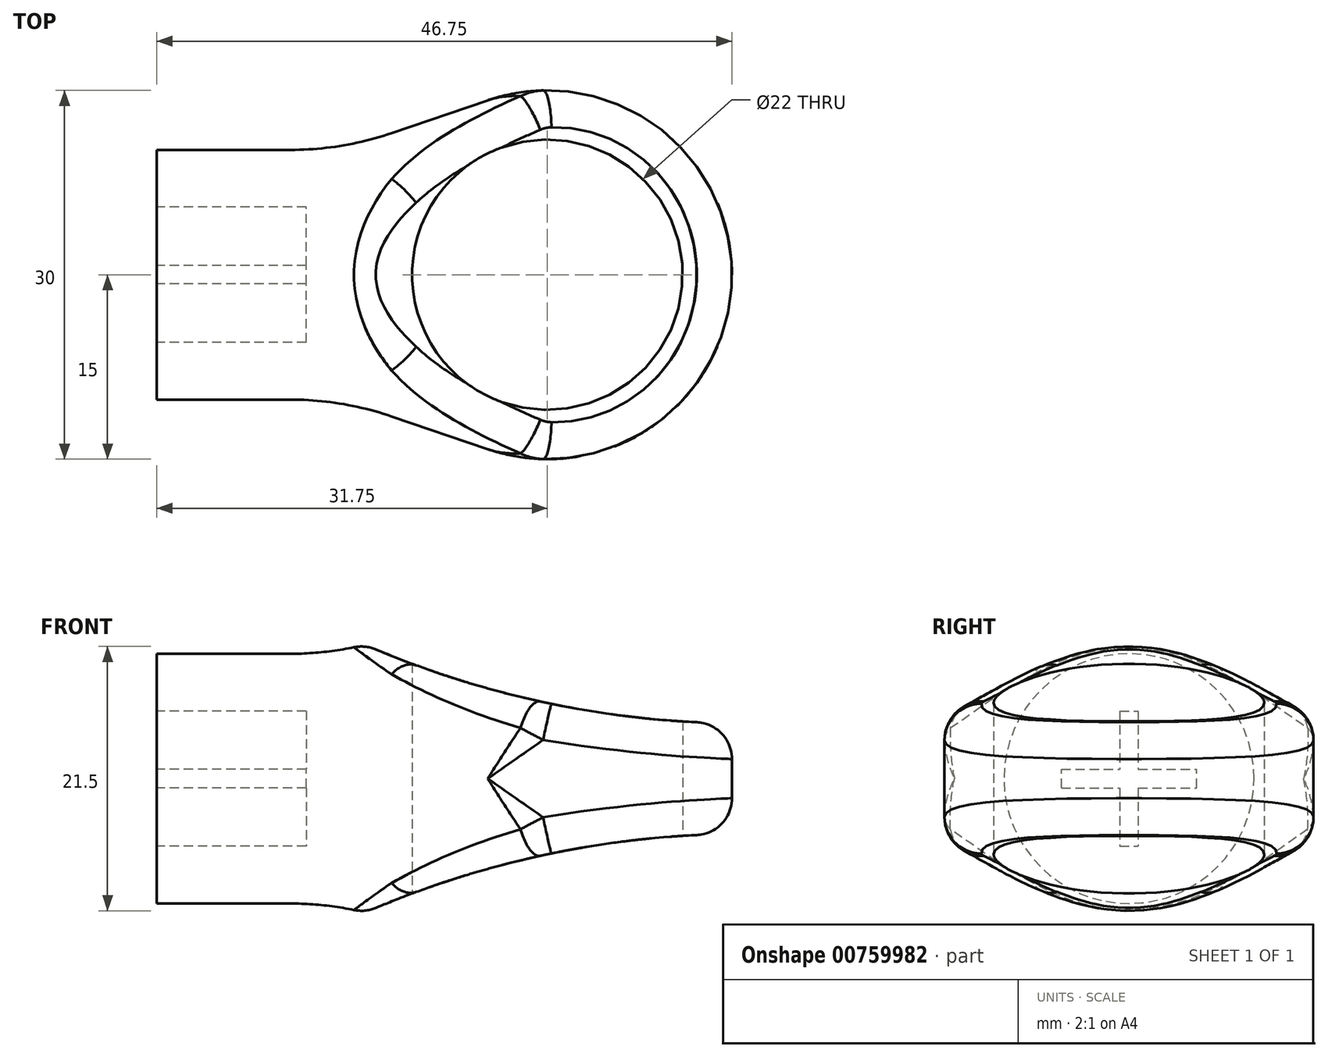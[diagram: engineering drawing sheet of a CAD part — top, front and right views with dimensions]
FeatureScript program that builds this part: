
annotation { "Feature Type Name" : "Feature", "Feature Type Description" : "" }
export const myFeature = defineFeature(function(context is Context, id is Id, definition is map)
    precondition{}
    {
        {
            var Q0;
            Q0=qCreatedBy(makeId("Top.planeOp"),FACE);
            var sketch = newSketch(context, id + "F0", { "sketchPlane" : qUnion([Q0])});
            skCircle(sketch, "E0", {"center": v(0, 0) * mm, "radius": 11 * mm});
            skCircle(sketch, "E1", {"center": v(0, 0) * mm, "radius": 15 * mm});
            skSolve(sketch);
        }
        {
            var Q0;
            Q0=makeQuery(id+"F0.imprint","IMPRINT",FACE,{"disambiguationData":[TD([[makeQuery(id+"F0.imprint","IMPRINT",EDGE,{"derivedFrom":sQuery(id+"F0.wireOp",EDGE,"E0")}),-1.0]])]});
            extrude(context, id + "F1", {"entities" : qUnion([Q0]), "endBound" : BoundingType.SYMMETRIC, "depth" : 25.4 * mm, "offsetDistance" : 25.4 * mm, "hasSecondDirection" : true, "secondDirectionOppositeDirection" : true, "secondDirectionDepth" : 4 * mm});
        }
        {
            var Q0;
            Q0=qCreatedBy(makeId("Front.planeOp"),FACE);
            var sketch = newSketch(context, id + "F2", { "sketchPlane" : qUnion([Q0])});
            skLineSegment(sketch, "E2.bottom", {"start": v(-11, 0) * mm, "end": v(-31.75, 0) * mm});
            skLineSegment(sketch, "E2.top", {"start": v(-16.66, 10.16) * mm, "end": v(-31.75, 10.16) * mm});
            skLineSegment(sketch, "E2.right", {"start": v(-31.75, 0) * mm, "end": v(-31.75, 10.16) * mm});
            skLineSegment(sketch, "E3", {"start": v(-11, 4.5) * mm, "end": v(-16.66, 10.16) * mm});
            skLineSegment(sketch, "E4", {"start": v(0, 4.5) * mm, "end": v(-11, 4.5) * mm, "construction": true});
            skLineSegment(sketch, "E5", {"start": v(-11, 4.5) * mm, "end": v(-11, 0) * mm});
            skSolve(sketch);
        }
        {
            var Q0;
            Q0=makeQuery(id+"F2.imprint","IMPRINT",FACE,{"disambiguationData":[TD([[makeQuery(id+"F2.imprint","IMPRINT",EDGE,{"derivedFrom":sQuery(id+"F2.wireOp",EDGE,"E2.bottom")}),-1.0]])]});
            var Q1;
            Q1=sQuery(id+"F2.wireOp",EDGE,"E2.bottom");
            revolve(context, id + "F3", {"operationType" : NewBodyOperationType.ADD, "surfaceOperationType" : NewSurfaceOperationType.NEW, "entities" : qUnion([Q0]), "axis" : qUnion([Q1]), "revolveType" : RevolveType.FULL});
        }
        {
            var Q0;
            Q0=qCreatedBy(makeId("Top.planeOp"),FACE);
            var sketch = newSketch(context, id + "F4", { "sketchPlane" : qUnion([Q0])});
            skLineSegment(sketch, "E6", {"start": v(-31.75, 10.16) * mm, "end": v(-16.66, 10.16) * mm, "construction": true});
            skLineSegment(sketch, "E7", {"start": v(-16.66, 10.16) * mm, "end": v(-13.35, 6.85) * mm, "construction": true});
            skArc(sketch, "E8.0.0", {"start": v(-13.84, 5.8) * mm, "mid": v(-15, 0) * mm, "end": v(-13.84, -5.8) * mm, "construction": true});
            skArc(sketch, "E8.0.2", {"start": v(-13.84, -5.8) * mm, "mid": v(15, 0) * mm, "end": v(-13.84, 5.8) * mm, "construction": true});
            skLineSegment(sketch, "E9", {"start": v(-16.66, 10.16) * mm, "end": v(-4.85, 14.2) * mm});
            skLineSegment(sketch, "E10", {"start": v(-16.66, 10.16) * mm, "end": v(-13.35, 6.85) * mm});
            skArc(sketch, "E11", {"start": v(-4.85, 14.2) * mm, "mid": v(-9.81, 11.35) * mm, "end": v(-13.35, 6.85) * mm});
            skLineSegment(sketch, "E12", {"start": v(-13.35, -6.85) * mm, "end": v(-16.66, -10.16) * mm, "construction": true});
            skLineSegment(sketch, "E13", {"start": v(-16.66, -10.16) * mm, "end": v(-4.85, -14.2) * mm});
            skLineSegment(sketch, "E14", {"start": v(-13.35, -6.85) * mm, "end": v(-16.66, -10.16) * mm});
            skArc(sketch, "E15", {"start": v(-13.35, -6.85) * mm, "mid": v(-9.81, -11.35) * mm, "end": v(-4.85, -14.2) * mm});
            skLineSegment(sketch, "E16", {"start": v(-16.66, -10.16) * mm, "end": v(-31.75, -10.16) * mm, "construction": true});
            skLineSegment(sketch, "E17", {"start": v(-16.66, 10.16) * mm, "end": v(-16.66, -10.16) * mm});
            skLineSegment(sketch, "E18", {"start": v(-13.35, 6.85) * mm, "end": v(-13.35, -6.85) * mm});
            skSolve(sketch);
        }
        {
            var Q0;
            Q0 = qSketchRegion(id + "F4", true);
            extrude(context, id + "F5", {"entities" : qUnion([Q0]), "operationType" : NewBodyOperationType.ADD, "endBound" : BoundingType.SYMMETRIC, "depth" : 25.4 * mm, "offsetDistance" : 25.4 * mm});
        }
        {
            var Q0;
            Q0=qCreatedBy(makeId("Top.planeOp"),FACE);
            var sketch = newSketch(context, id + "F6", { "sketchPlane" : qUnion([Q0])});
            skLineSegment(sketch, "E19", {"start": v(-31.75, 10.16) * mm, "end": v(-16.66, 10.16) * mm, "construction": true});
            skLineSegment(sketch, "E20.0.0", {"start": v(-16.66, -10.16) * mm, "end": v(-4.85, -14.2) * mm, "construction": true});
            skArc(sketch, "E20.0.1", {"start": v(-4.85, -14.2) * mm, "mid": v(15, 0) * mm, "end": v(-4.85, 14.2) * mm, "construction": true});
            skLineSegment(sketch, "E20.0.2", {"start": v(-4.85, 14.2) * mm, "end": v(-16.66, 10.16) * mm, "construction": true});
            skLineSegment(sketch, "E20.0.3", {"start": v(-16.66, 10.16) * mm, "end": v(-16.66, 9.1) * mm, "construction": true});
            skFitSpline(sketch, "E20.0.4", {"points": [v(-16.66, 9.1) * mm, v(-16.05, 8.43) * mm, v(-15.16, 7.4) * mm, v(-14, 6) * mm, v(-13.16, 4.93) * mm, v(-12.38, 3.81) * mm, v(-11.8, 2.84) * mm, v(-11.42, 2.01) * mm, v(-11.19, 1.36) * mm, v(-11.04, 0.7) * mm, v(-11, 0.23) * mm, v(-11, 0) * mm], "construction": true});
            skCircle(sketch, "E20.0.5", {"center": v(0, 0) * mm, "radius": 11 * mm, "construction": true});
            skFitSpline(sketch, "E20.0.6", {"points": [v(-11, 0) * mm, v(-11, -0.23) * mm, v(-11.03, -0.68) * mm, v(-11.18, -1.35) * mm, v(-11.41, -2) * mm, v(-11.8, -2.82) * mm, v(-12.37, -3.8) * mm, v(-13.16, -4.92) * mm, v(-14, -6) * mm, v(-15.15, -7.4) * mm, v(-16.05, -8.43) * mm, v(-16.66, -9.1) * mm], "construction": true});
            skLineSegment(sketch, "E20.0.7", {"start": v(-16.66, -9.1) * mm, "end": v(-16.66, -10.16) * mm, "construction": true});
            skLineSegment(sketch, "E21", {"start": v(-16.66, 10.16) * mm, "end": v(1.72, 16.44) * mm});
            skLineSegment(sketch, "E22", {"start": v(1.72, 16.44) * mm, "end": v(1.72, 19.36) * mm});
            skLineSegment(sketch, "E23", {"start": v(1.72, 19.36) * mm, "end": v(-16.66, 19.36) * mm});
            skLineSegment(sketch, "E24", {"start": v(-16.66, 19.36) * mm, "end": v(-16.66, 10.16) * mm});
            skLineSegment(sketch, "E25", {"start": v(0, 0) * mm, "end": v(-37.39, 0) * mm});
            skSolve(sketch);
        }
        {
            var Q0;
            Q0=makeQuery(id+"F6.imprint","IMPRINT",FACE,{"disambiguationData":[TD([[makeQuery(id+"F6.imprint","IMPRINT",EDGE,{"derivedFrom":sQuery(id+"F6.wireOp",EDGE,"E21")}),1.0]])]});
            var Q1;
            Q1=sQuery(id+"F6.wireOp",EDGE,"E25");
            revolve(context, id + "F7", {"operationType" : NewBodyOperationType.REMOVE, "surfaceOperationType" : NewSurfaceOperationType.NEW, "entities" : qUnion([Q0]), "axis" : qUnion([Q1]), "revolveType" : RevolveType.FULL, "oppositeDirection" : true});
        }
        {
            var Q0;
            Q0=makeQuery(id+"F3.opRevolve","SWEPT_FACE",FACE,{"disambiguationData":[OSD([sQuery(id+"F2.wireOp",EDGE,"E2.right")])]});
            var sketch = newSketch(context, id + "F8", { "sketchPlane" : qUnion([Q0])});
            skLineSegment(sketch, "E26.bottom", {"start": v(5.5, -0.75) * mm, "end": v(-5.5, -0.75) * mm});
            skLineSegment(sketch, "E26.top", {"start": v(5.5, 0.75) * mm, "end": v(-5.5, 0.75) * mm});
            skLineSegment(sketch, "E26.left", {"start": v(5.5, -0.75) * mm, "end": v(5.5, 0.75) * mm});
            skLineSegment(sketch, "E26.right", {"start": v(-5.5, -0.75) * mm, "end": v(-5.5, 0.75) * mm});
            skPoint(sketch, "E26.middle", {"position": v(0, 0) * mm});
            skLineSegment(sketch, "E27.bottom", {"start": v(0.75, 5.5) * mm, "end": v(-0.75, 5.5) * mm});
            skLineSegment(sketch, "E27.top", {"start": v(0.75, -5.5) * mm, "end": v(-0.75, -5.5) * mm});
            skLineSegment(sketch, "E27.left", {"start": v(0.75, 5.5) * mm, "end": v(0.75, -5.5) * mm});
            skLineSegment(sketch, "E27.right", {"start": v(-0.75, 5.5) * mm, "end": v(-0.75, -5.5) * mm});
            skSolve(sketch);
        }
        {
            var Q0;
            Q0 = qSketchRegion(id + "F8", true);
            extrude(context, id + "F9", {"entities" : qUnion([Q0]), "operationType" : NewBodyOperationType.REMOVE, "oppositeDirection" : true, "depth" : 12.14 * mm, "offsetDistance" : 25.4 * mm});
        }
        {
            var Q0;
            {var subQ0=sQuery(id+"F2.wireOp",EDGE,"E3");var subQ1=makeQuery(id+"F3.opRevolve","SWEPT_FACE",FACE,{"disambiguationData":[OSD([subQ0])]});var subQ2=sQuery(id+"F2.wireOp",EDGE,"E2.top");var subQ3=makeQuery(id+"F3.opRevolve","SWEPT_FACE",FACE,{"disambiguationData":[OSD([subQ2])]});var subQ4=sQuery(id+"F4.wireOp",EDGE,"E9");var subQ5=makeQuery(id+"F5.opExtrude","SWEPT_FACE",FACE,{"disambiguationData":[OSD([subQ4])]});var subQ6=sQuery(id+"F0.wireOp",EDGE,"E1");var subQ7=sQuery(id+"F0.wireOp",EDGE,"E0");var subQ8=sQuery(id+"F4.wireOp",EDGE,"E17");var subQ9=makeQuery(id+"F5.opExtrude","SWEPT_FACE",FACE,{"disambiguationData":[OSD([subQ8])]});var subQ10=sQuery(id+"F4.wireOp",EDGE,"E18");var subQ11=sQuery(id+"F4.wireOp",EDGE,"E15");var subQ12=sQuery(id+"F4.wireOp",EDGE,"E13");var subQ13=sQuery(id+"F4.wireOp",EDGE,"E11");var subQ14=makeQuery(id+"F3.opRevolve","SWEPT_EDGE",EDGE,{"disambiguationData":[OSD([subQ2,subQ0])]});Q0=makeQuery(id+"F7.boolean.opBoolean","MERGE",EDGE,{"derivedFrom":[makeQuery(id+"F5.boolean.opBoolean","SPLIT",EDGE,{"disambiguationData":[topologyDisambiguationEdgeConnected([subQ3,subQ9]),TD([makeQuery(id+"F1.opExtrude","CAP_FACE",FACE,{"disambiguationData":[OSD([subQ7,subQ6])],"isStart":true}),subQ3,subQ1,subQ5,makeQuery(id+"F5.opExtrude","CAP_FACE",FACE,{"disambiguationData":[OSD([subQ4,subQ13,subQ12,subQ11,subQ10,subQ8])],"isStart":true}),subQ9])],"derivedFrom":subQ14}),makeQuery(id+"F5.boolean.opBoolean","SPLIT",EDGE,{"disambiguationData":[topologyDisambiguationEdgeConnected([subQ3,subQ9]),TD([makeQuery(id+"F1.opExtrude","CAP_FACE",FACE,{"disambiguationData":[OSD([subQ7,subQ6])],"isStart":false}),subQ3,subQ1,subQ5,makeQuery(id+"F5.opExtrude","CAP_FACE",FACE,{"disambiguationData":[OSD([subQ4,subQ13,subQ12,subQ11,subQ10,subQ8])],"isStart":false}),subQ9])],"derivedFrom":subQ14}),makeQuery(id+"F7.opRevolve","SWEPT_EDGE",EDGE,{"disambiguationData":[OSD([sQuery(id+"F6.wireOp",EDGE,"E21"),sQuery(id+"F6.wireOp",EDGE,"E24")])]})]});}
            var Q1;
            {var subQ0=sQuery(id+"F4.wireOp",EDGE,"E17");var subQ1=sQuery(id+"F4.wireOp",EDGE,"E18");var subQ2=sQuery(id+"F4.wireOp",EDGE,"E15");var subQ3=sQuery(id+"F4.wireOp",EDGE,"E13");var subQ4=sQuery(id+"F4.wireOp",EDGE,"E11");var subQ5=sQuery(id+"F4.wireOp",EDGE,"E9");var subQ6=sQuery(id+"F2.wireOp",EDGE,"E3");var subQ7=makeQuery(id+"F3.opRevolve","SWEPT_FACE",FACE,{"disambiguationData":[OSD([subQ6])]});var subQ8=sQuery(id+"F2.wireOp",EDGE,"E2.top");var subQ9=makeQuery(id+"F3.opRevolve","SWEPT_FACE",FACE,{"disambiguationData":[OSD([subQ8])]});var subQ10=sQuery(id+"F0.wireOp",EDGE,"E1");var subQ11=sQuery(id+"F0.wireOp",EDGE,"E0");var subQ12=makeQuery(id+"F5.opExtrude","SWEPT_FACE",FACE,{"disambiguationData":[OSD([subQ0])]});var subQ13=makeQuery(id+"F5.opExtrude","SWEPT_FACE",FACE,{"disambiguationData":[OSD([subQ3])]});var subQ14=makeQuery(id+"F3.opRevolve","SWEPT_EDGE",EDGE,{"disambiguationData":[OSD([subQ8,subQ6])]});Q1=makeQuery(id+"F7.boolean.opBoolean","MERGE",EDGE,{"derivedFrom":[makeQuery(id+"F5.boolean.opBoolean","SPLIT",EDGE,{"disambiguationData":[topologyDisambiguationEdgeConnected([subQ9,subQ12]),TD([makeQuery(id+"F1.opExtrude","CAP_FACE",FACE,{"disambiguationData":[OSD([subQ11,subQ10])],"isStart":true}),subQ9,subQ7,makeQuery(id+"F5.opExtrude","CAP_FACE",FACE,{"disambiguationData":[OSD([subQ5,subQ4,subQ3,subQ2,subQ1,subQ0])],"isStart":true}),subQ13,subQ12])],"derivedFrom":subQ14}),makeQuery(id+"F5.boolean.opBoolean","SPLIT",EDGE,{"disambiguationData":[topologyDisambiguationEdgeConnected([subQ9,subQ12]),TD([makeQuery(id+"F1.opExtrude","CAP_FACE",FACE,{"disambiguationData":[OSD([subQ11,subQ10])],"isStart":false}),subQ9,subQ7,makeQuery(id+"F5.opExtrude","CAP_FACE",FACE,{"disambiguationData":[OSD([subQ5,subQ4,subQ3,subQ2,subQ1,subQ0])],"isStart":false}),subQ13,subQ12])],"derivedFrom":subQ14}),makeQuery(id+"F7.opRevolve","SWEPT_EDGE",EDGE,{"disambiguationData":[OSD([sQuery(id+"F6.wireOp",EDGE,"E21"),sQuery(id+"F6.wireOp",EDGE,"E24")])]})]});}
            fillet(context, id + "F10", {"entities" : qUnion([Q0, Q1]), "radius" : 25.4 * mm, "tangentPropagation" : true, "allowEdgeOverflow" : false});
        }
        {
            var Q0;
            Q0=qCreatedBy(makeId("Front.planeOp"),FACE);
            var sketch = newSketch(context, id + "F11", { "sketchPlane" : qUnion([Q0])});
            skLineSegment(sketch, "E28.bottom", {"start": v(19.05, -4.5) * mm, "end": v(-19.05, -4.5) * mm, "construction": true});
            skLineSegment(sketch, "E28.top", {"start": v(19.05, 4.5) * mm, "end": v(-19.05, 4.5) * mm, "construction": true});
            skLineSegment(sketch, "E28.left", {"start": v(19.05, -4.5) * mm, "end": v(19.05, 4.5) * mm, "construction": true});
            skLineSegment(sketch, "E28.right", {"start": v(-19.05, -4.5) * mm, "end": v(-19.05, 4.5) * mm, "construction": true});
            skPoint(sketch, "E28.middle", {"position": v(0, 0) * mm});
            skArc(sketch, "E29", {"start": v(-19.67, 13.2) * mm, "mid": v(-2.42, 6.7) * mm, "end": v(15.87, 4.5) * mm});
            skLineSegment(sketch, "E30", {"start": v(15.88, 4.5) * mm, "end": v(15.88, 13.2) * mm});
            skLineSegment(sketch, "E31", {"start": v(15.88, 13.2) * mm, "end": v(-19.67, 13.2) * mm});
            skLineSegment(sketch, "E32", {"start": v(21.62, 0) * mm, "end": v(-15.27, 0) * mm, "construction": true});
            skPoint(sketch, "E32.startSnap0", {"position": v(19.05, 0) * mm});
            skArc(sketch, "E33.MirrorCS", {"start": v(-19.67, -13.2) * mm, "mid": v(-2.42, -6.7) * mm, "end": v(15.87, -4.5) * mm});
            skLineSegment(sketch, "E34.MirrorCS", {"start": v(15.88, -4.5) * mm, "end": v(15.88, -13.2) * mm});
            skLineSegment(sketch, "E35.MirrorCS", {"start": v(15.88, -13.2) * mm, "end": v(-19.67, -13.2) * mm});
            skSolve(sketch);
        }
        {
            var Q0;
            Q0 = qSketchRegion(id + "F11", true);
            extrude(context, id + "F12", {"entities" : qUnion([Q0]), "operationType" : NewBodyOperationType.REMOVE, "endBound" : BoundingType.SYMMETRIC, "depth" : 51.3 * mm, "offsetDistance" : 25.4 * mm});
        }
        {
            var Q0;
            Q0=makeQuery(id+"F7.boolean.opBoolean","INTERSECT",EDGE,{"disambiguationData":[OD(2.0)],"derivedFrom":[makeQuery(id+"F1.opExtrude","SWEPT_FACE",FACE,{"disambiguationData":[OSD([sQuery(id+"F0.wireOp",EDGE,"E1")])]}),makeQuery(id+"F7.opRevolve","SWEPT_FACE",FACE,{"disambiguationData":[OSD([sQuery(id+"F6.wireOp",EDGE,"E21")])]})]});
            var Q1;
            Q1=makeQuery(id+"F7.boolean.opBoolean","INTERSECT",EDGE,{"disambiguationData":[OD(3.0)],"derivedFrom":[makeQuery(id+"F1.opExtrude","SWEPT_FACE",FACE,{"disambiguationData":[OSD([sQuery(id+"F0.wireOp",EDGE,"E1")])]}),makeQuery(id+"F7.opRevolve","SWEPT_FACE",FACE,{"disambiguationData":[OSD([sQuery(id+"F6.wireOp",EDGE,"E21")])]})]});
            var Q2;
            Q2=makeQuery(id+"F7.boolean.opBoolean","INTERSECT",EDGE,{"disambiguationData":[OD(0.0)],"derivedFrom":[makeQuery(id+"F1.opExtrude","SWEPT_FACE",FACE,{"disambiguationData":[OSD([sQuery(id+"F0.wireOp",EDGE,"E1")])]}),makeQuery(id+"F7.opRevolve","SWEPT_FACE",FACE,{"disambiguationData":[OSD([sQuery(id+"F6.wireOp",EDGE,"E21")])]})]});
            var Q3;
            Q3=makeQuery(id+"F7.boolean.opBoolean","INTERSECT",EDGE,{"disambiguationData":[OD(1.0)],"derivedFrom":[makeQuery(id+"F1.opExtrude","SWEPT_FACE",FACE,{"disambiguationData":[OSD([sQuery(id+"F0.wireOp",EDGE,"E1")])]}),makeQuery(id+"F7.opRevolve","SWEPT_FACE",FACE,{"disambiguationData":[OSD([sQuery(id+"F6.wireOp",EDGE,"E21")])]})]});
            fillet(context, id + "F13", {"entities" : qUnion([Q0, Q1, Q2, Q3]), "radius" : 5.08 * mm, "tangentPropagation" : true, "allowEdgeOverflow" : false});
        }
        {
            var Q0;
            Q0=makeQuery(id+"F12.boolean.opBoolean","INTERSECT",EDGE,{"derivedFrom":[makeQuery(id+"F1.opExtrude","SWEPT_FACE",FACE,{"disambiguationData":[OSD([sQuery(id+"F0.wireOp",EDGE,"E1")])]}),makeQuery(id+"F12.opExtrude","SWEPT_FACE",FACE,{"disambiguationData":[OSD([sQuery(id+"F11.wireOp",EDGE,"E33.MirrorCS")])]})]});
            var Q1;
            Q1=makeQuery(id+"F12.boolean.opBoolean","INTERSECT",EDGE,{"derivedFrom":[makeQuery(id+"F1.opExtrude","SWEPT_FACE",FACE,{"disambiguationData":[OSD([sQuery(id+"F0.wireOp",EDGE,"E1")])]}),makeQuery(id+"F12.opExtrude","SWEPT_FACE",FACE,{"disambiguationData":[OSD([sQuery(id+"F11.wireOp",EDGE,"E29")])]})]});
            fillet(context, id + "F14", {"entities" : qUnion([Q0, Q1]), "radius" : 3 * mm, "tangentPropagation" : true, "allowEdgeOverflow" : false});
        }
    });
